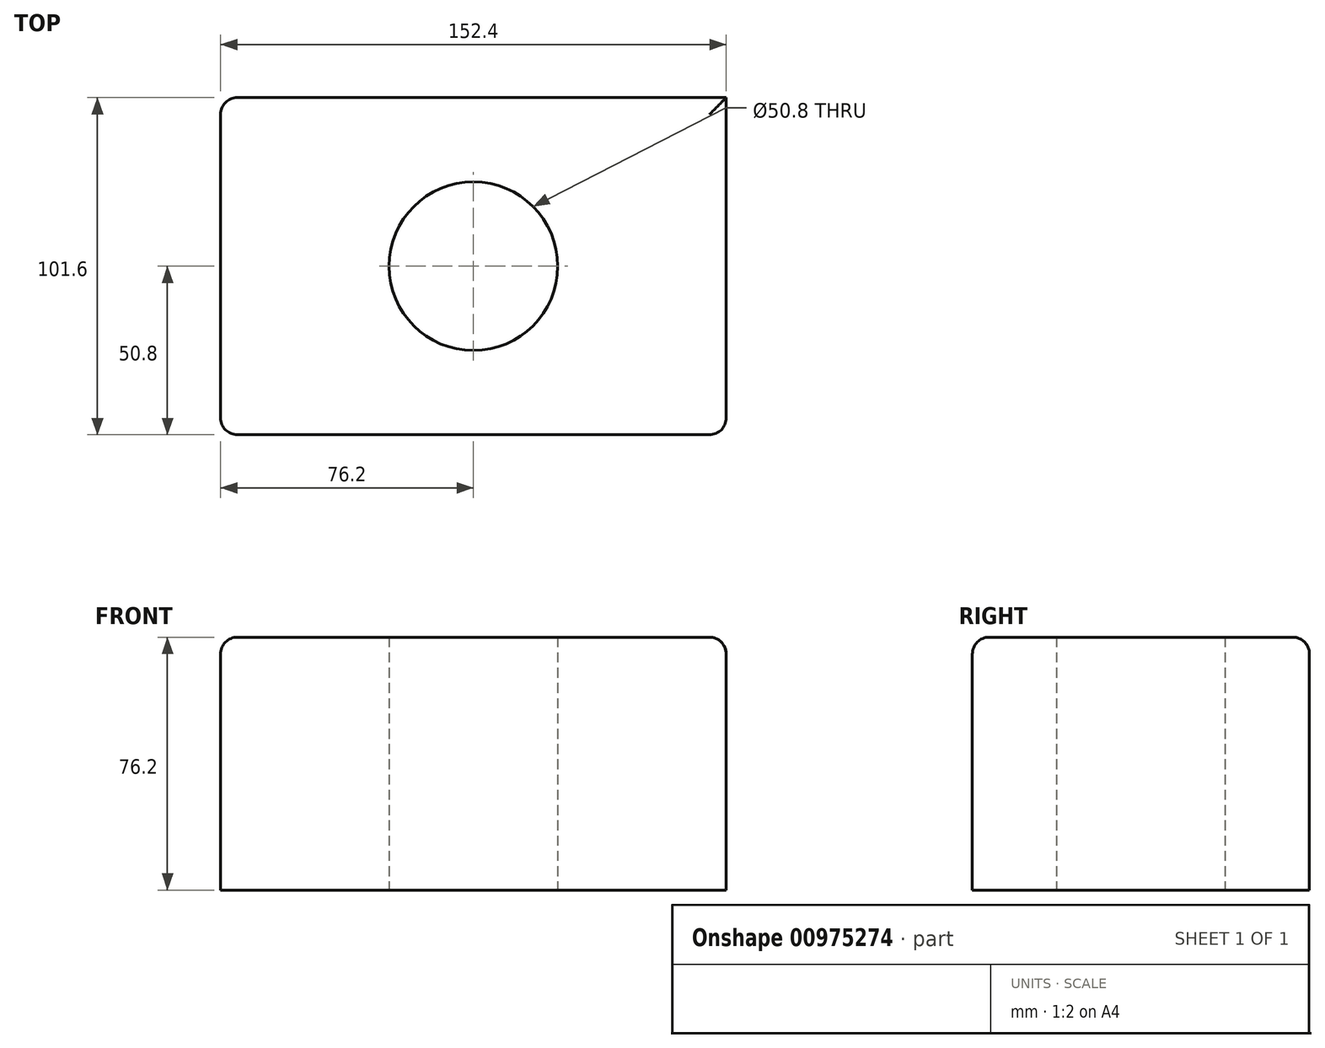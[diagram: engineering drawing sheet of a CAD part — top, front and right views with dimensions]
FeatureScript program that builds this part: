
annotation { "Feature Type Name" : "Feature", "Feature Type Description" : "" }
export const myFeature = defineFeature(function(context is Context, id is Id, definition is map)
    precondition{}
    {
        {
            var Q0;
            Q0=qCreatedBy(makeId("Top.planeOp"),FACE);
            var sketch = newSketch(context, id + "F0", { "sketchPlane" : qUnion([Q0])});
            skLineSegment(sketch, "E0.bottom", {"start": v(-76.2, 50.8) * mm, "end": v(76.2, 50.8) * mm});
            skLineSegment(sketch, "E0.top", {"start": v(-76.2, -50.8) * mm, "end": v(76.2, -50.8) * mm});
            skLineSegment(sketch, "E0.left", {"start": v(-76.2, 50.8) * mm, "end": v(-76.2, -50.8) * mm});
            skLineSegment(sketch, "E0.right", {"start": v(76.2, 50.8) * mm, "end": v(76.2, -50.8) * mm});
            skPoint(sketch, "E0.middle", {"position": v(0, 0) * mm});
            skCircle(sketch, "E1", {"center": v(0, 0) * mm, "radius": 25.4 * mm});
            skSolve(sketch);
        }
        {
            var Q0;
            Q0=makeQuery(id+"F0.imprint","IMPRINT",FACE,{"disambiguationData":[TD([[makeQuery(id+"F0.imprint","IMPRINT",EDGE,{"derivedFrom":sQuery(id+"F0.wireOp",EDGE,"E0.bottom")}),-1.0]])]});
            extrude(context, id + "F1", {"entities" : qUnion([Q0]), "depth" : 76.2 * mm, "offsetDistance" : 25.4 * mm});
        }
        {
            var Q0;
            Q0=makeQuery(id+"F1.opExtrude","CAP_EDGE",EDGE,{"disambiguationData":[OSD([sQuery(id+"F0.wireOp",EDGE,"E0.left")])],"isStart":false});
            fillet(context, id + "F2", {"entities" : qUnion([Q0]), "radius" : 5.08 * mm, "tangentPropagation" : true, "allowEdgeOverflow" : false});
        }
        {
            var Q0;
            Q0=makeQuery(id+"F1.opExtrude","CAP_EDGE",EDGE,{"disambiguationData":[OSD([sQuery(id+"F0.wireOp",EDGE,"E0.bottom")])],"isStart":false});
            var Q1;
            Q1=makeQuery(id+"F1.opExtrude","CAP_EDGE",EDGE,{"disambiguationData":[OSD([sQuery(id+"F0.wireOp",EDGE,"E0.right")])],"isStart":false});
            var Q2;
            Q2=makeQuery(id+"F1.opExtrude","CAP_EDGE",EDGE,{"disambiguationData":[OSD([sQuery(id+"F0.wireOp",EDGE,"E0.top")])],"isStart":false});
            fillet(context, id + "F3", {"entities" : qUnion([Q0, Q1, Q2]), "radius" : 5.08 * mm, "tangentPropagation" : true, "allowEdgeOverflow" : false});
        }
        {
            var Q0;
            Q0=makeQuery(id+"F1.opExtrude","SWEPT_EDGE",EDGE,{"disambiguationData":[OSD([sQuery(id+"F0.wireOp",EDGE,"E0.top"),sQuery(id+"F0.wireOp",EDGE,"E0.right")])]});
            fillet(context, id + "F4", {"entities" : qUnion([Q0]), "radius" : 5.08 * mm, "tangentPropagation" : true, "allowEdgeOverflow" : false});
        }
    });
